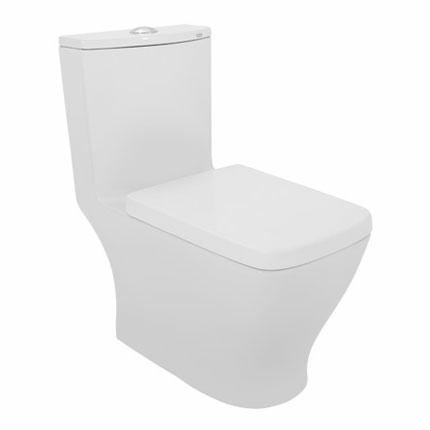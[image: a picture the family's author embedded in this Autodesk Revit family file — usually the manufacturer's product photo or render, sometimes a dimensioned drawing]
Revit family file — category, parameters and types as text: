
# Revit family: OP CAPRI PLUS
name_source: partatom
category: Aparatos sanitarios
units: mm (PartAtom-declared; Revit-internal decimal feet)

## family parameters
Compartido = Sí
Corte con vacíos al cargar = No
Cota de conector redondo = Diámetro de uso
Número OmniClass = 23.45.00.00
Punto de cálculo de habitación = No
Se basa en plano de trabajo = Sí
Siempre vertical = Sí
Tipo de pieza = Normal
Título OmniClass = Sanitary, Laundry, and Cleaning Equipment

## types (1)
- OP CAPRI PLUS
    Accessories = Paquete de fijación, sello de cera, reducción para válvula de admisión de Ø15/16-14 NS-1 a ½-14 NPSM
    Características del Producto = DCerámica de alto brillo, grado de calidad "A", espesor grueso en la cerámica para mayor resistencia.
    Comentarios de tipo = Inodoro One piece Capri Plus, con trampa oculta y asiento de cierre lento. Descarga 4.8L
    Descripción = OP CAPRI PLUS Inodoro One piece Capri Plus, con trampa oculta y asiento de cierre lento. Descarga 4.8L
    Elevación por defecto = 0.0"
    Fabricante = Helvex S.A. de C.V.
    Imagen de tipo = OP CAPRI PLUS.jpg
    Materials = Cerámica porcelanizada de alto brillo, calidad "A", Tipo l
    Modelo = OP CAPRI PLUS
    Presión Máxima de Trabajo = 85.3 psi
    Presión Mínima de Trabajo = 3.5 psi
    URL = https://www.helvex.com.mx
    Valves = Val. de admisión y descarga certificadas, val. de admisión silenciosa, válvulas armadas y calibradas, válvulas de descarga con sello hermético

## geometry (parser evidence)
native form markers: Sweep x3
no freeform markers — native parametric forms only
